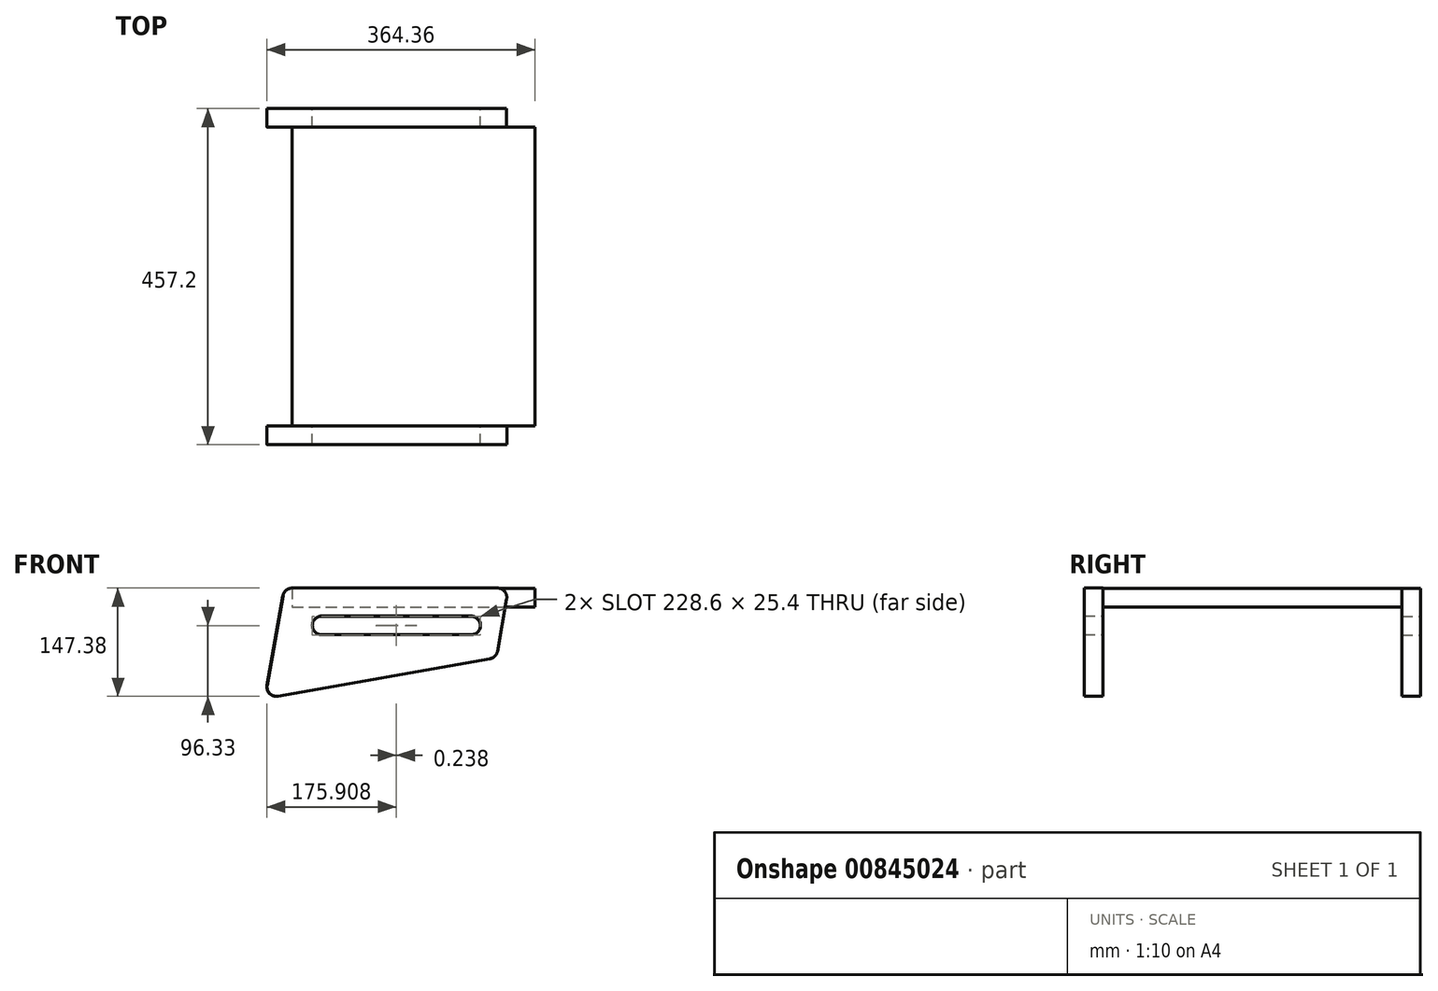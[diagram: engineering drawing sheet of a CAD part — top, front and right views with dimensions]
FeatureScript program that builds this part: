
annotation { "Feature Type Name" : "Feature", "Feature Type Description" : "" }
export const myFeature = defineFeature(function(context is Context, id is Id, definition is map)
    precondition{}
    {
        {
            var Q0;
            Q0=qCreatedBy(makeId("Front.planeOp"),FACE);
            var sketch = newSketch(context, id + "F0", { "sketchPlane" : qUnion([Q0])});
            skLineSegment(sketch, "E0", {"start": v(-116.54, 63.5) * mm, "end": v(162.47, 63.5) * mm});
            skLineSegment(sketch, "E1", {"start": v(174.98, 48.6) * mm, "end": v(162.47, -22.36) * mm});
            skLineSegment(sketch, "E2", {"start": v(152.17, -32.66) * mm, "end": v(-135.8, -83.44) * mm});
            skLineSegment(sketch, "E3", {"start": v(-150.5, -68.72) * mm, "end": v(-129.04, 53) * mm});
            skLineSegment(sketch, "E4.bottom", {"start": v(-76.4, 25.4) * mm, "end": v(126.8, 25.4) * mm});
            skLineSegment(sketch, "E4.top", {"start": v(-76.4, 0) * mm, "end": v(126.8, 0) * mm});
            skLineSegment(sketch, "E4.left", {"start": v(-89.1, 12.7) * mm, "end": v(-89.1, 12.7) * mm});
            skLineSegment(sketch, "E4.right", {"start": v(139.5, 12.7) * mm, "end": v(139.5, 12.7) * mm});
            skLineSegment(sketch, "E5", {"start": v(-89.1, 25.4) * mm, "end": v(-89.1, 63.5) * mm, "construction": true});
            skLineSegment(sketch, "E6", {"start": v(-89.1, 63.5) * mm, "end": v(-127.2, 63.5) * mm, "construction": true});
            skPoint(sketch, "E7.visualSharp", {"position": v(139.5, 25.4) * mm});
            skArc(sketch, "E7.filletArc", {"start": v(139.5, 12.7) * mm, "mid": v(135.79, 21.68) * mm, "end": v(126.8, 25.4) * mm});
            skPoint(sketch, "E8.visualSharp", {"position": v(139.5, 0) * mm});
            skArc(sketch, "E8.filletArc", {"start": v(126.8, 0) * mm, "mid": v(135.79, 3.72) * mm, "end": v(139.5, 12.7) * mm});
            skPoint(sketch, "E9.visualSharp", {"position": v(-89.1, 0) * mm});
            skArc(sketch, "E9.filletArc", {"start": v(-89.1, 12.7) * mm, "mid": v(-85.37, 3.72) * mm, "end": v(-76.4, 0) * mm});
            skPoint(sketch, "E10.visualSharp", {"position": v(-89.1, 25.4) * mm});
            skArc(sketch, "E10.filletArc", {"start": v(-76.4, 25.4) * mm, "mid": v(-85.37, 21.68) * mm, "end": v(-89.1, 12.7) * mm});
            skPoint(sketch, "E11.visualSharp", {"position": v(-153.66, -86.58) * mm});
            skArc(sketch, "E11.filletArc", {"start": v(-150.5, -68.72) * mm, "mid": v(-146.98, -79.9) * mm, "end": v(-135.8, -83.44) * mm});
            skPoint(sketch, "E12.visualSharp", {"position": v(-127.2, 63.5) * mm});
            skArc(sketch, "E12.filletArc", {"start": v(-116.54, 63.5) * mm, "mid": v(-124.7, 60.53) * mm, "end": v(-129.04, 53) * mm});
            skPoint(sketch, "E13.visualSharp", {"position": v(177.6, 63.5) * mm});
            skArc(sketch, "E13.filletArc", {"start": v(174.98, 48.6) * mm, "mid": v(172.2, 58.96) * mm, "end": v(162.47, 63.5) * mm});
            skPoint(sketch, "E14.visualSharp", {"position": v(160.92, -31.12) * mm});
            skArc(sketch, "E14.filletArc", {"start": v(152.17, -32.66) * mm, "mid": v(158.94, -29.13) * mm, "end": v(162.47, -22.36) * mm});
            skSolve(sketch);
        }
        {
            var Q0;
            Q0=makeQuery(id+"F0.imprint","IMPRINT",FACE,{"disambiguationData":[TD([[makeQuery(id+"F0.imprint","IMPRINT",EDGE,{"derivedFrom":sQuery(id+"F0.wireOp",EDGE,"E0")}),-1.0]])]});
            extrude(context, id + "F1", {"entities" : qUnion([Q0]), "depth" : 25.4 * mm, "offsetDistance" : 25.4 * mm});
        }
        {
            var Q0;
            Q0=makeQuery(id+"F1.opExtrude","CAP_FACE",FACE,{"disambiguationData":[OSD([sQuery(id+"F0.wireOp",EDGE,"E0"),sQuery(id+"F0.wireOp",EDGE,"E1"),sQuery(id+"F0.wireOp",EDGE,"E2"),sQuery(id+"F0.wireOp",EDGE,"E3"),sQuery(id+"F0.wireOp",EDGE,"E4.bottom"),sQuery(id+"F0.wireOp",EDGE,"E4.top"),sQuery(id+"F0.wireOp",EDGE,"E7.filletArc"),sQuery(id+"F0.wireOp",EDGE,"E8.filletArc"),sQuery(id+"F0.wireOp",EDGE,"E9.filletArc"),sQuery(id+"F0.wireOp",EDGE,"E10.filletArc"),sQuery(id+"F0.wireOp",EDGE,"E11.filletArc"),sQuery(id+"F0.wireOp",EDGE,"E12.filletArc"),sQuery(id+"F0.wireOp",EDGE,"E13.filletArc"),sQuery(id+"F0.wireOp",EDGE,"E14.filletArc")])],"isStart":false});
            var sketch = newSketch(context, id + "F2", { "sketchPlane" : qUnion([Q0])});
            skLineSegment(sketch, "E15.bottom", {"start": v(-116.54, 63.5) * mm, "end": v(213.66, 63.5) * mm});
            skLineSegment(sketch, "E15.top", {"start": v(-116.54, 38.1) * mm, "end": v(213.66, 38.1) * mm});
            skLineSegment(sketch, "E15.left", {"start": v(-116.54, 63.5) * mm, "end": v(-116.54, 38.1) * mm});
            skLineSegment(sketch, "E15.right", {"start": v(213.66, 63.5) * mm, "end": v(213.66, 38.1) * mm});
            skSolve(sketch);
        }
        {
            var Q0;
            Q0 = qSketchRegion(id + "F2", true);
            extrude(context, id + "F3", {"entities" : qUnion([Q0]), "depth" : 406.4 * mm, "offsetDistance" : 25.4 * mm});
        }
        {
            var Q0;
            Q0=makeQuery(id+"F3.opExtrude","CAP_FACE",FACE,{"disambiguationData":[OSD([sQuery(id+"F2.wireOp",EDGE,"E15.bottom"),sQuery(id+"F2.wireOp",EDGE,"E15.top"),sQuery(id+"F2.wireOp",EDGE,"E15.left"),sQuery(id+"F2.wireOp",EDGE,"E15.right")])],"isStart":false});
            var sketch = newSketch(context, id + "F4", { "sketchPlane" : qUnion([Q0])});
            skLineSegment(sketch, "E16", {"start": v(-116.3, 63.75) * mm, "end": v(162.71, 63.75) * mm});
            skLineSegment(sketch, "E17", {"start": v(175.22, 48.84) * mm, "end": v(162.7, -22.11) * mm});
            skLineSegment(sketch, "E18", {"start": v(152.4, -32.41) * mm, "end": v(-135.56, -83.19) * mm});
            skLineSegment(sketch, "E19", {"start": v(-150.27, -68.48) * mm, "end": v(-128.8, 53.25) * mm});
            skLineSegment(sketch, "E20.bottom", {"start": v(-76.15, 25.65) * mm, "end": v(127.05, 25.65) * mm});
            skLineSegment(sketch, "E20.top", {"start": v(-76.15, 0.25) * mm, "end": v(127.05, 0.25) * mm});
            skLineSegment(sketch, "E20.left", {"start": v(-88.85, 12.95) * mm, "end": v(-88.85, 12.95) * mm});
            skLineSegment(sketch, "E20.right", {"start": v(139.75, 12.95) * mm, "end": v(139.75, 12.95) * mm});
            skLineSegment(sketch, "E21", {"start": v(-88.85, 25.65) * mm, "end": v(-88.85, 63.75) * mm, "construction": true});
            skLineSegment(sketch, "E22", {"start": v(-88.85, 63.75) * mm, "end": v(-126.95, 63.75) * mm, "construction": true});
            skPoint(sketch, "E23.visualSharp", {"position": v(139.75, 25.65) * mm});
            skArc(sketch, "E23.filletArc", {"start": v(139.75, 12.95) * mm, "mid": v(136.03, 21.93) * mm, "end": v(127.05, 25.65) * mm});
            skPoint(sketch, "E24.visualSharp", {"position": v(139.75, 0.25) * mm});
            skArc(sketch, "E24.filletArc", {"start": v(127.05, 0.25) * mm, "mid": v(136.03, 3.97) * mm, "end": v(139.75, 12.95) * mm});
            skPoint(sketch, "E25.visualSharp", {"position": v(-88.85, 0.25) * mm});
            skArc(sketch, "E25.filletArc", {"start": v(-88.85, 12.95) * mm, "mid": v(-85.13, 3.97) * mm, "end": v(-76.15, 0.25) * mm});
            skPoint(sketch, "E26.visualSharp", {"position": v(-88.85, 25.65) * mm});
            skArc(sketch, "E26.filletArc", {"start": v(-76.15, 25.65) * mm, "mid": v(-85.13, 21.93) * mm, "end": v(-88.85, 12.95) * mm});
            skPoint(sketch, "E27.visualSharp", {"position": v(-153.42, -86.34) * mm});
            skArc(sketch, "E27.filletArc", {"start": v(-150.27, -68.48) * mm, "mid": v(-146.74, -79.66) * mm, "end": v(-135.56, -83.19) * mm});
            skPoint(sketch, "E28.visualSharp", {"position": v(-126.95, 63.75) * mm});
            skArc(sketch, "E28.filletArc", {"start": v(-116.3, 63.75) * mm, "mid": v(-124.46, 60.77) * mm, "end": v(-128.8, 53.25) * mm});
            skPoint(sketch, "E29.visualSharp", {"position": v(177.85, 63.75) * mm});
            skArc(sketch, "E29.filletArc", {"start": v(175.22, 48.84) * mm, "mid": v(172.44, 59.2) * mm, "end": v(162.71, 63.75) * mm});
            skPoint(sketch, "E30.visualSharp", {"position": v(161.16, -30.87) * mm});
            skArc(sketch, "E30.filletArc", {"start": v(152.4, -32.41) * mm, "mid": v(159.18, -28.89) * mm, "end": v(162.7, -22.11) * mm});
            skSolve(sketch);
        }
        {
            var Q0;
            {var subQ0=sQuery(id+"F4.wireOp",EDGE,"E16");Q0=makeQuery(id+"F4.imprint","IMPRINT",FACE,{"disambiguationData":[TD([[makeQuery(id+"F4.imprint","IMPRINT",EDGE,{"derivedFrom":subQ0}),-1.0]])]});}
            var Q1;
            {var subQ0=makeQuery(id+"F3.opExtrude","CAP_EDGE",EDGE,{"disambiguationData":[OSD([sQuery(id+"F2.wireOp",EDGE,"E15.left")])],"isStart":false});Q1=makeQuery(id+"F4.imprint","IMPRINT",FACE,{"disambiguationData":[TD([[makeQuery(id+"F4.imprint","IMPRINT",EDGE,{"derivedFrom":subQ0}),1.0]])]});}
            extrude(context, id + "F5", {"entities" : qUnion([Q0, Q1]), "depth" : 25.4 * mm, "offsetDistance" : 25.4 * mm});
        }
    });
